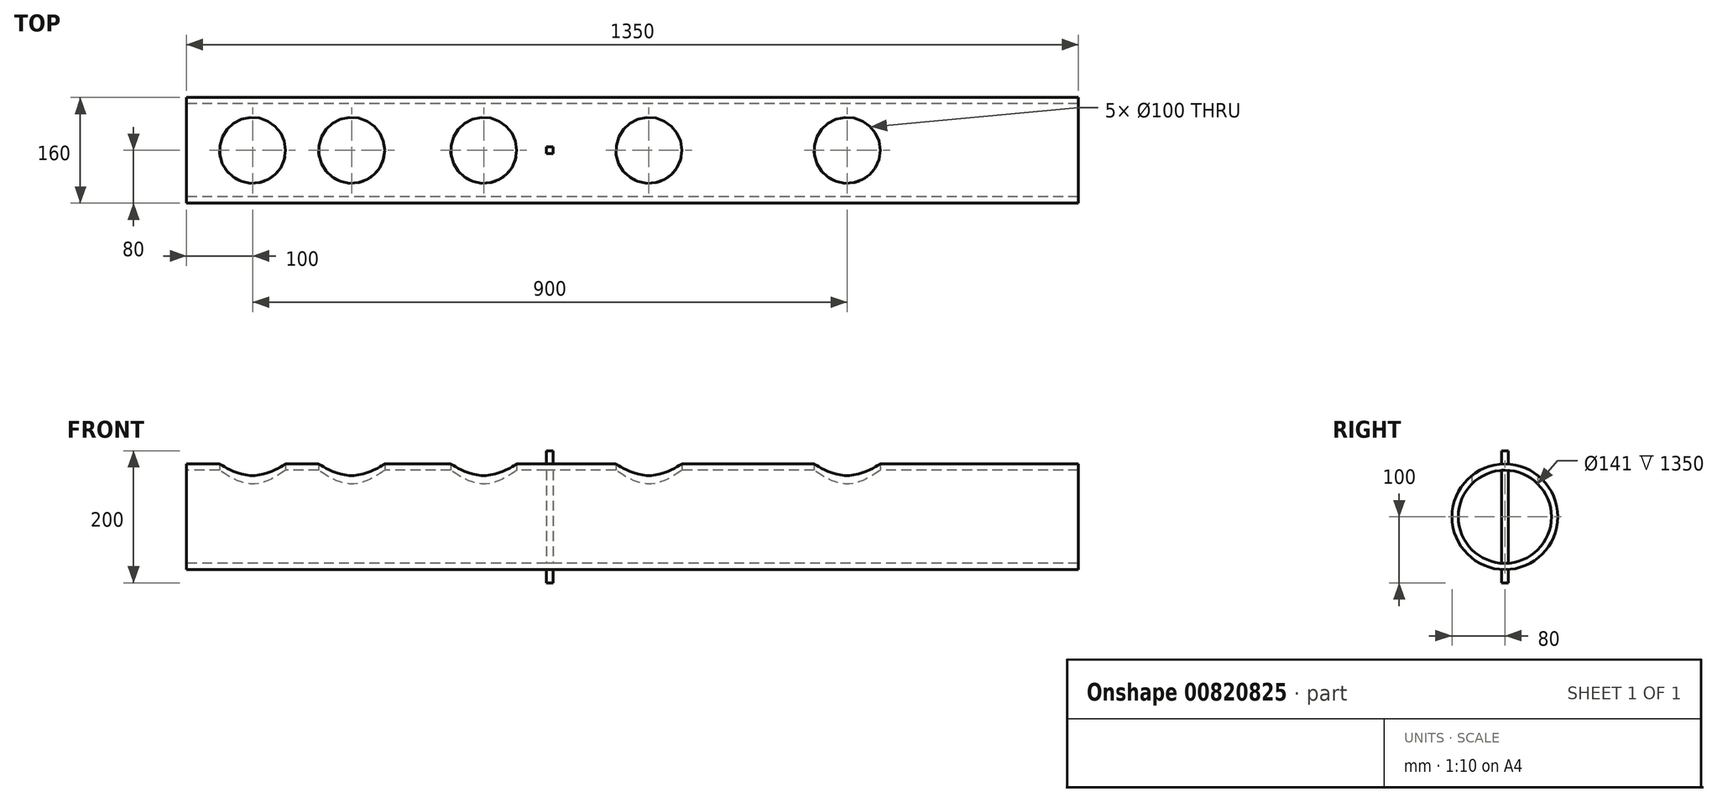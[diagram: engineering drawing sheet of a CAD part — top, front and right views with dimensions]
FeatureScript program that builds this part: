
annotation { "Feature Type Name" : "Feature", "Feature Type Description" : "" }
export const myFeature = defineFeature(function(context is Context, id is Id, definition is map)
    precondition{}
    {
        {
            var Q0;
            Q0=qCreatedBy(makeId("Right.planeOp"),FACE);
            var sketch = newSketch(context, id + "F0", { "sketchPlane" : qUnion([Q0])});
            skCircle(sketch, "E0", {"center": v(0, 0) * mm, "radius": 80 * mm});
            skCircle(sketch, "E1", {"center": v(0, 0) * mm, "radius": 70.5 * mm});
            skSolve(sketch);
        }
        {
            var Q0;
            Q0=qSketchRegion(id+"F0",true);
            extrude(context, id + "F1", {"entities" : qUnion([Q0]), "depth" : 1350 * mm, "offsetDistance" : 25 * mm});
        }
        {
            var Q0;
            Q0=qCreatedBy(makeId("Top.planeOp"),FACE);
            var sketch = newSketch(context, id + "F2", { "sketchPlane" : qUnion([Q0])});
            skLineSegment(sketch, "E2", {"start": v(0, 0) * mm, "end": v(1100, 0) * mm});
            skLineSegment(sketch, "E3", {"start": v(1100, 0) * mm, "end": v(1151.8, -193.18) * mm});
            skLineSegment(sketch, "E4", {"start": v(0, 0) * mm, "end": v(100, 0) * mm});
            skCircle(sketch, "E5", {"center": v(100, 0) * mm, "radius": 50 * mm});
            skLineSegment(sketch, "E6", {"start": v(100, 0) * mm, "end": v(250, 0) * mm});
            skLineSegment(sketch, "E7", {"start": v(250, 0) * mm, "end": v(450, 0) * mm});
            skLineSegment(sketch, "E8", {"start": v(450, 0) * mm, "end": v(700, 0) * mm});
            skLineSegment(sketch, "E9", {"start": v(700, 0) * mm, "end": v(1000, 0) * mm});
            skCircle(sketch, "E10", {"center": v(250, 0) * mm, "radius": 50 * mm});
            skCircle(sketch, "E11", {"center": v(450, 0) * mm, "radius": 50 * mm});
            skCircle(sketch, "E12", {"center": v(700, 0) * mm, "radius": 50 * mm});
            skCircle(sketch, "E13", {"center": v(1000, 0) * mm, "radius": 50 * mm});
            skPoint(sketch, "E14.middle", {"position": v(0, 0) * mm});
            skLineSegment(sketch, "E15", {"start": v(0, 0) * mm, "end": v(0, 130) * mm});
            skLineSegment(sketch, "E16", {"start": v(0, 0) * mm, "end": v(0, -130) * mm});
            skPoint(sketch, "E17.orphan", {"position": v(75, -130) * mm});
            skPoint(sketch, "E18.orphan", {"position": v(75, 130) * mm});
            skArc(sketch, "E19", {"start": v(-35.75, 130) * mm, "mid": v(-50, 0) * mm, "end": v(-35.75, -130) * mm});
            skLineSegment(sketch, "E20", {"start": v(-35.75, 130) * mm, "end": v(0, 130) * mm});
            skLineSegment(sketch, "E21", {"start": v(0, -130) * mm, "end": v(-35.75, -130) * mm});
            skPoint(sketch, "E22.middle", {"position": v(570, 0) * mm});
            skSolve(sketch);
        }
        {
            var Q0;
            {var subQ0=sQuery(id+"F2.wireOp",EDGE,"E6");var subQ1=sQuery(id+"F2.wireOp",EDGE,"E4");var subQ2=makeQuery(id+"F2.imprint","INTERSECT",VERTEX,{"derivedFrom":[subQ1,subQ0]});Q0=makeQuery(id+"F2.imprint","IMPRINT",FACE,{"disambiguationData":[TD([[makeQuery(id+"F2.imprint","IMPRINT",EDGE,{"disambiguationData":[TD([[subQ2,1.0]])],"derivedFrom":subQ1}),-1.0]])]});}
            var Q1;
            {var subQ0=sQuery(id+"F2.wireOp",EDGE,"E6");var subQ1=sQuery(id+"F2.wireOp",EDGE,"E4");var subQ2=makeQuery(id+"F2.imprint","INTERSECT",VERTEX,{"derivedFrom":[subQ1,subQ0]});Q1=makeQuery(id+"F2.imprint","IMPRINT",FACE,{"disambiguationData":[TD([[makeQuery(id+"F2.imprint","IMPRINT",EDGE,{"disambiguationData":[TD([[subQ2,1.0]])],"derivedFrom":subQ1}),1.0]])]});}
            var Q2;
            {var subQ0=sQuery(id+"F2.wireOp",EDGE,"E7");var subQ1=sQuery(id+"F2.wireOp",EDGE,"E6");var subQ2=makeQuery(id+"F2.imprint","INTERSECT",VERTEX,{"derivedFrom":[subQ1,subQ0]});Q2=makeQuery(id+"F2.imprint","IMPRINT",FACE,{"disambiguationData":[TD([[makeQuery(id+"F2.imprint","IMPRINT",EDGE,{"disambiguationData":[TD([[subQ2,1.0]])],"derivedFrom":subQ1}),1.0]])]});}
            var Q3;
            {var subQ0=sQuery(id+"F2.wireOp",EDGE,"E7");var subQ1=sQuery(id+"F2.wireOp",EDGE,"E6");var subQ2=makeQuery(id+"F2.imprint","INTERSECT",VERTEX,{"derivedFrom":[subQ1,subQ0]});Q3=makeQuery(id+"F2.imprint","IMPRINT",FACE,{"disambiguationData":[TD([[makeQuery(id+"F2.imprint","IMPRINT",EDGE,{"disambiguationData":[TD([[subQ2,1.0]])],"derivedFrom":subQ1}),-1.0]])]});}
            var Q4;
            {var subQ0=sQuery(id+"F2.wireOp",EDGE,"E8");var subQ1=sQuery(id+"F2.wireOp",EDGE,"E7");var subQ2=makeQuery(id+"F2.imprint","INTERSECT",VERTEX,{"derivedFrom":[subQ1,subQ0]});Q4=makeQuery(id+"F2.imprint","IMPRINT",FACE,{"disambiguationData":[TD([[makeQuery(id+"F2.imprint","IMPRINT",EDGE,{"disambiguationData":[TD([[subQ2,1.0]])],"derivedFrom":subQ1}),1.0]])]});}
            var Q5;
            {var subQ0=sQuery(id+"F2.wireOp",EDGE,"E8");var subQ1=sQuery(id+"F2.wireOp",EDGE,"E7");var subQ2=makeQuery(id+"F2.imprint","INTERSECT",VERTEX,{"derivedFrom":[subQ1,subQ0]});Q5=makeQuery(id+"F2.imprint","IMPRINT",FACE,{"disambiguationData":[TD([[makeQuery(id+"F2.imprint","IMPRINT",EDGE,{"disambiguationData":[TD([[subQ2,1.0]])],"derivedFrom":subQ1}),-1.0]])]});}
            var Q6;
            {var subQ0=sQuery(id+"F2.wireOp",EDGE,"E9");var subQ1=sQuery(id+"F2.wireOp",EDGE,"E8");var subQ2=makeQuery(id+"F2.imprint","INTERSECT",VERTEX,{"derivedFrom":[subQ1,subQ0]});Q6=makeQuery(id+"F2.imprint","IMPRINT",FACE,{"disambiguationData":[TD([[makeQuery(id+"F2.imprint","IMPRINT",EDGE,{"disambiguationData":[TD([[subQ2,1.0]])],"derivedFrom":subQ1}),1.0]])]});}
            var Q7;
            {var subQ0=sQuery(id+"F2.wireOp",EDGE,"E9");var subQ1=sQuery(id+"F2.wireOp",EDGE,"E8");var subQ2=makeQuery(id+"F2.imprint","INTERSECT",VERTEX,{"derivedFrom":[subQ1,subQ0]});Q7=makeQuery(id+"F2.imprint","IMPRINT",FACE,{"disambiguationData":[TD([[makeQuery(id+"F2.imprint","IMPRINT",EDGE,{"disambiguationData":[TD([[subQ2,1.0]])],"derivedFrom":subQ1}),-1.0]])]});}
            var Q8;
            {var subQ0=sQuery(id+"F2.wireOp",EDGE,"E9");var subQ1=sQuery(id+"F2.wireOp",EDGE,"E2");var subQ2=makeQuery(id+"F2.imprint","INTERSECT",VERTEX,{"derivedFrom":[subQ1,subQ0]});Q8=makeQuery(id+"F2.imprint","IMPRINT",FACE,{"disambiguationData":[TD([[makeQuery(id+"F2.imprint","IMPRINT",EDGE,{"disambiguationData":[TD([[subQ2,-1.0]])],"derivedFrom":subQ1}),1.0]])]});}
            var Q9;
            {var subQ0=sQuery(id+"F2.wireOp",EDGE,"E9");var subQ1=sQuery(id+"F2.wireOp",EDGE,"E2");var subQ2=makeQuery(id+"F2.imprint","INTERSECT",VERTEX,{"derivedFrom":[subQ1,subQ0]});Q9=makeQuery(id+"F2.imprint","IMPRINT",FACE,{"disambiguationData":[TD([[makeQuery(id+"F2.imprint","IMPRINT",EDGE,{"disambiguationData":[TD([[subQ2,-1.0]])],"derivedFrom":subQ1}),-1.0]])]});}
            extrude(context, id + "F3", {"entities" : qUnion([Q0, Q1, Q2, Q3, Q4, Q5, Q6, Q7, Q8, Q9]), "operationType" : NewBodyOperationType.REMOVE, "depth" : 200 * mm, "offsetDistance" : 25 * mm});
        }
        {
            var Q0;
            Q0=qCreatedBy(makeId("Top.planeOp"),FACE);
            var sketch = newSketch(context, id + "F4", { "sketchPlane" : qUnion([Q0])});
            skLineSegment(sketch, "E23", {"start": v(0, 0) * mm, "end": v(550, 0) * mm});
            skLineSegment(sketch, "E24.bottom", {"start": v(555, -5) * mm, "end": v(545, -5) * mm});
            skLineSegment(sketch, "E24.top", {"start": v(555, 5) * mm, "end": v(545, 5) * mm});
            skLineSegment(sketch, "E24.left", {"start": v(555, -5) * mm, "end": v(555, 5) * mm});
            skLineSegment(sketch, "E24.right", {"start": v(545, -5) * mm, "end": v(545, 5) * mm});
            skPoint(sketch, "E24.middle", {"position": v(550, 0) * mm});
            skSolve(sketch);
        }
        {
            var Q0;
            Q0=qSketchRegion(id+"F4",true);
            extrude(context, id + "F5", {"entities" : qUnion([Q0]), "operationType" : NewBodyOperationType.ADD, "endBound" : BoundingType.SYMMETRIC, "depth" : 200 * mm, "offsetDistance" : 25 * mm});
        }
    });
